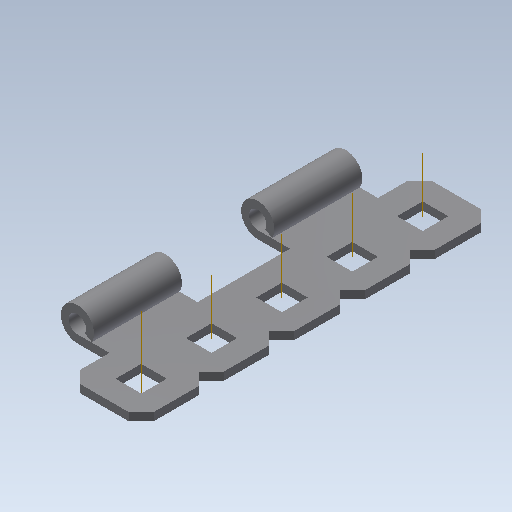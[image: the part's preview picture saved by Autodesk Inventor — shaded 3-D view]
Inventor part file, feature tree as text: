
AUTODESK INVENTOR PART (.ipt)
format: ipt  version: 2020 (Build 240168000, 168)  size: 169,984 bytes
history: native  units: in
note: dims shown in document units (in); Inventor stores cm internally (conversion verified against a paired STEP export)
features: other x8, pattern_linear x1, imported_body x1
ambient origin geometry x8: Origin, YZ Plane, XZ Plane, XY Plane, X Axis, Y Axis, Z Axis, Center Point
bodies: Body1 (feature_tree)
feature tree (10):
  other  "Cut-Extrude3"
  other  "Hinge Plate"
  other  "axis"
  pattern_linear  "axes"  Count1=5 Spacing1=0.5in
  imported_body  "Base1"
  other  "Work Point1"
  other  "Work Axis2"
  other  "Work Axis3"
  other  "Work Axis4"
  other  "Work Axis5"
